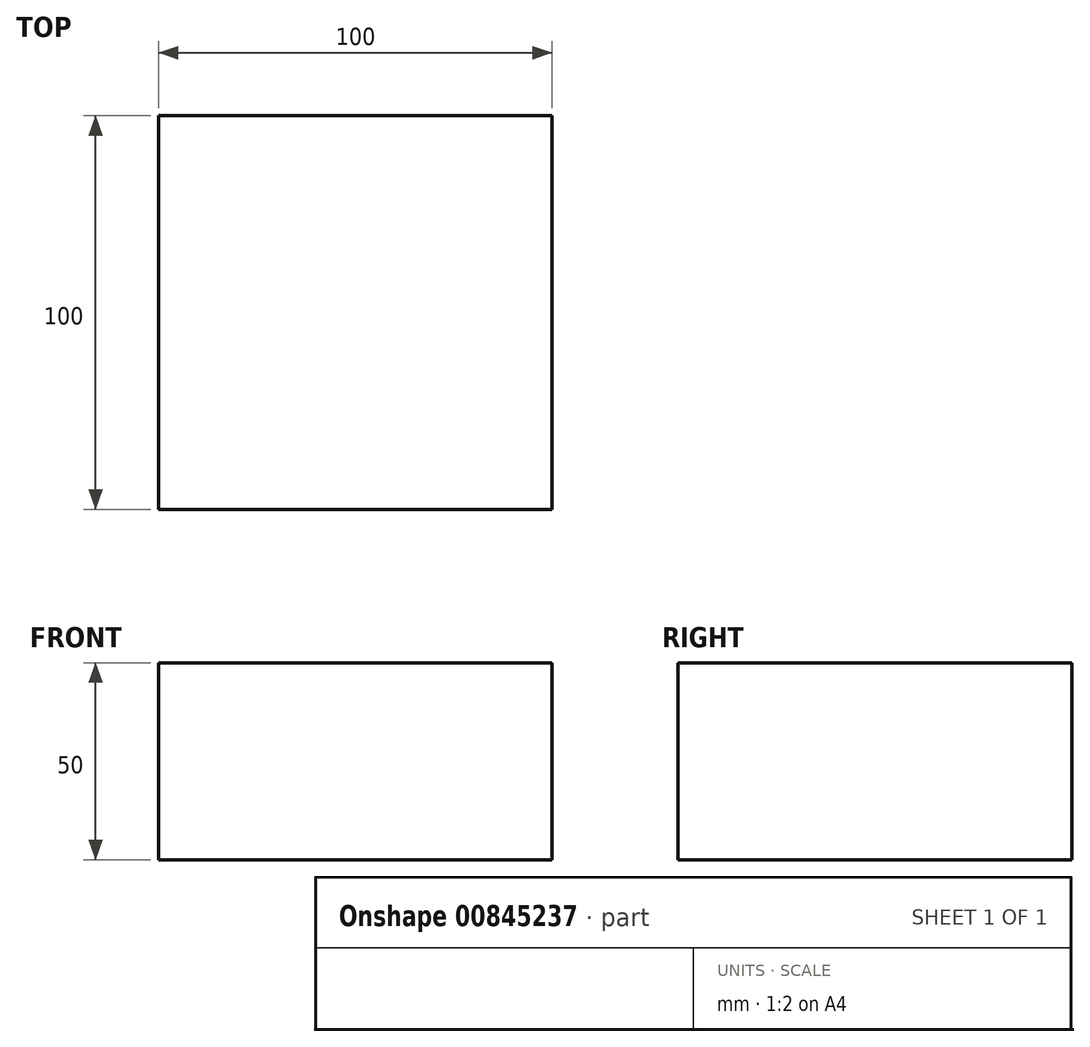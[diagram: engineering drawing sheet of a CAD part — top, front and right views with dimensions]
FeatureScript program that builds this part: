
annotation { "Feature Type Name" : "Feature", "Feature Type Description" : "" }
export const myFeature = defineFeature(function(context is Context, id is Id, definition is map)
    precondition{}
    {
        {
            var Q0;
            Q0=qCreatedBy(makeId("Top.planeOp"),FACE);
            var sketch = newSketch(context, id + "F0", { "sketchPlane" : qUnion([Q0])});
            skLineSegment(sketch, "E0.bottom", {"start": v(-50, 50) * mm, "end": v(50, 50) * mm});
            skLineSegment(sketch, "E0.top", {"start": v(-50, -50) * mm, "end": v(50, -50) * mm});
            skLineSegment(sketch, "E0.left", {"start": v(-50, 50) * mm, "end": v(-50, -50) * mm});
            skLineSegment(sketch, "E0.right", {"start": v(50, 50) * mm, "end": v(50, -50) * mm});
            skSolve(sketch);
        }
        {
            var Q0;
            Q0=makeQuery(id+"F0.imprint","IMPRINT",FACE,{"disambiguationData":[TD([[makeQuery(id+"F0.imprint","IMPRINT",EDGE,{"derivedFrom":sQuery(id+"F0.wireOp",EDGE,"E0.bottom")}),-1.0]])]});
            extrude(context, id + "F1", {"entities" : qUnion([Q0]), "depth" : 50 * mm, "offsetDistance" : 25 * mm});
        }
    });
